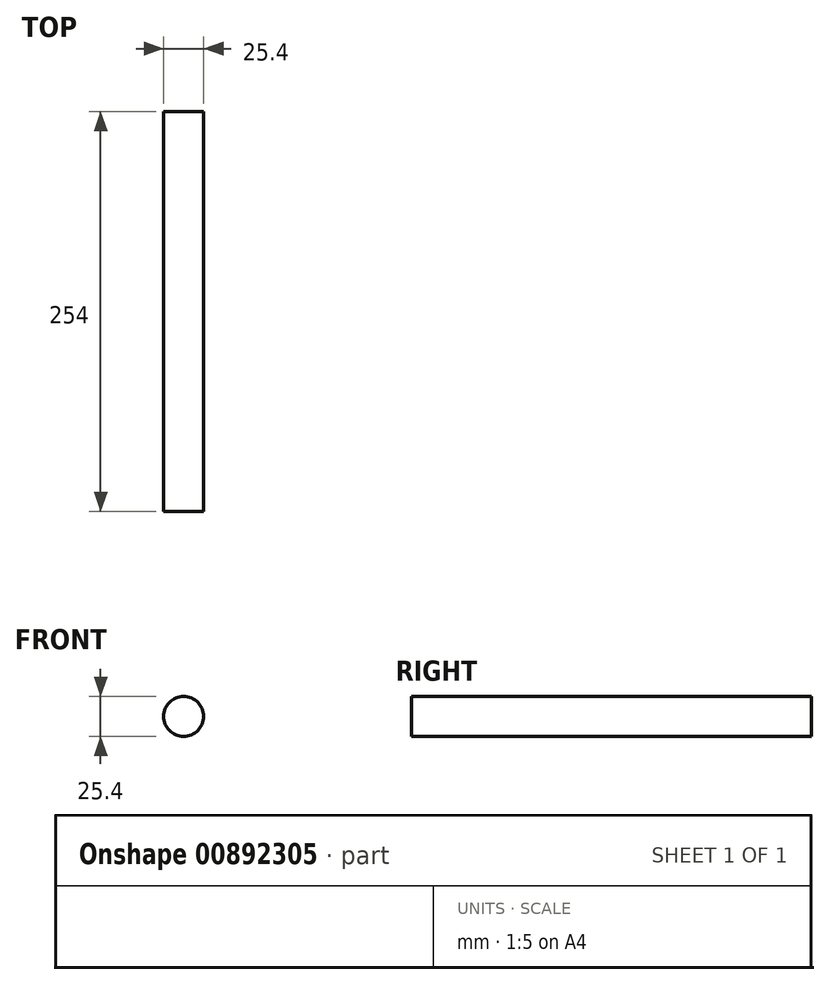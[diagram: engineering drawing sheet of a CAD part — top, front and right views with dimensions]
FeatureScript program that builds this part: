
annotation { "Feature Type Name" : "Feature", "Feature Type Description" : "" }
export const myFeature = defineFeature(function(context is Context, id is Id, definition is map)
    precondition{}
    {
        {
            var Q0;
            Q0=qCreatedBy(makeId("Front.planeOp"),FACE);
            var sketch = newSketch(context, id + "F0", { "sketchPlane" : qUnion([Q0])});
            skCircle(sketch, "E0", {"center": v(0, 0) * mm, "radius": 12.7 * mm});
            skSolve(sketch);
        }
        {
            var Q0;
            Q0 = qSketchRegion(id + "F0", true);
            extrude(context, id + "F1", {"entities" : qUnion([Q0]), "depth" : 254 * mm, "offsetDistance" : 25.4 * mm});
        }
    });
